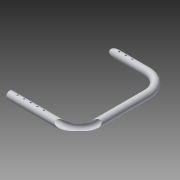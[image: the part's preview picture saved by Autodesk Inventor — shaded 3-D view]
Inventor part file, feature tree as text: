
AUTODESK INVENTOR PART (.ipt)
format: ipt  version: 2015 (Build 190159000, 159)  size: 274,432 bytes
history: native  units: mm
features: other x7, sketch x3, reference x2, sweep x1, hole x1, projected_geometry x1
ambient origin geometry x8: Origin, YZ Plane, XZ Plane, XY Plane, X Axis, Y Axis, Z Axis, Center Point
bodies: Body1 (feature_tree)
feature tree (15):
  other  "Bryła1"
  other  "Płaszczyzna konstrukcyjna1"
  sketch  "Szkic1"
  other  "Płaszczyzna konstrukcyjna2"
  sweep  "Przeciągnięcie1"
  other  "Płaszczyzna konstrukcyjna3"
  hole  "Otwór1"  [1 undecoded]
  other  "Płaszczyzna konstrukcyjna4"
  other  "Płaszczyzna konstrukcyjna5"
  reference  "Odniesienie1"
  sketch  "Szkic2"
  reference  "Odniesienie2"
  sketch  "Szkic3"
  projected_geometry  "Pętla rzutowana1"
  other  "Rzutuj krawędzie tnące1"
note: 1 required parameter value undecoded (feature->parameter linkage not recoverable at this tier; creation-order binding heuristic only, values carry confidence <= 0.55)
